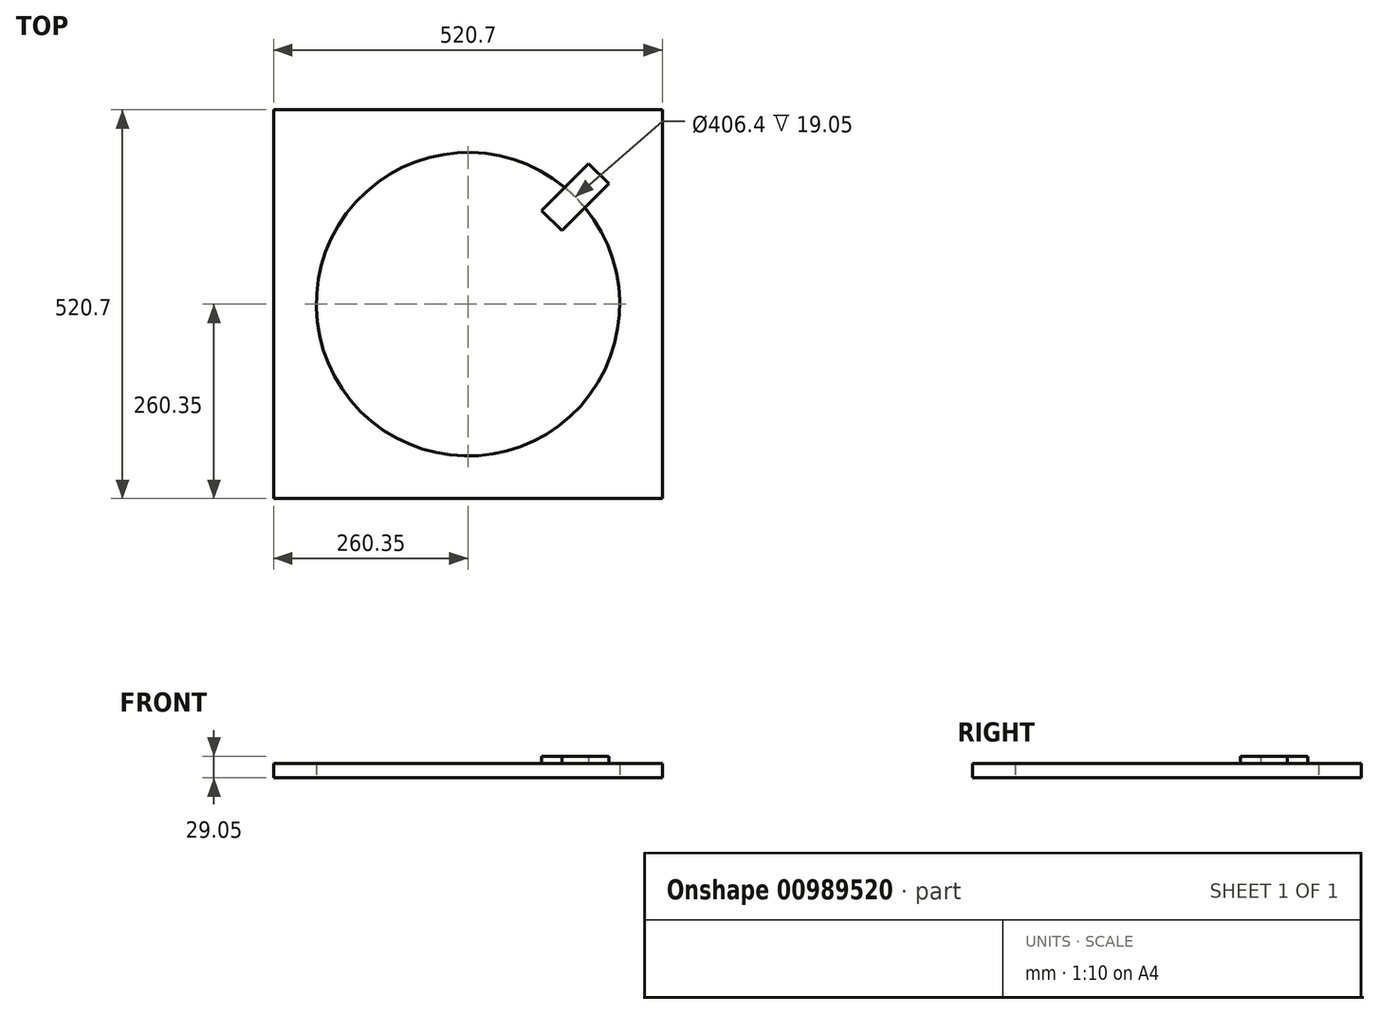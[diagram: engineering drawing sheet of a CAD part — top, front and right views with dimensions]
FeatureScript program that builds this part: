
annotation { "Feature Type Name" : "Feature", "Feature Type Description" : "" }
export const myFeature = defineFeature(function(context is Context, id is Id, definition is map)
    precondition{}
    {
        {
            var Q0;
            Q0=qCreatedBy(makeId("Top.planeOp"),FACE);
            var sketch = newSketch(context, id + "F0", { "sketchPlane" : qUnion([Q0])});
            skLineSegment(sketch, "E0.bottom", {"start": v(-260.35, -260.35) * mm, "end": v(260.35, -260.35) * mm});
            skLineSegment(sketch, "E0.top", {"start": v(-260.35, 260.35) * mm, "end": v(260.35, 260.35) * mm});
            skLineSegment(sketch, "E0.left", {"start": v(-260.35, -260.35) * mm, "end": v(-260.35, 260.35) * mm});
            skLineSegment(sketch, "E0.right", {"start": v(260.35, -260.35) * mm, "end": v(260.35, 260.35) * mm});
            skPoint(sketch, "E0.middle", {"position": v(0, 0) * mm});
            skCircle(sketch, "E1", {"center": v(0, 0) * mm, "radius": 203.2 * mm});
            skSolve(sketch);
        }
        {
            var Q0;
            Q0 = qSketchRegion(id + "F0", true);
            extrude(context, id + "F1", {"entities" : qUnion([Q0]), "depth" : 19.05 * mm, "offsetDistance" : 25.4 * mm});
        }
        {
            var Q0;
            Q0=makeQuery(id+"F1.opExtrude","CAP_FACE",FACE,{"disambiguationData":[OSD([sQuery(id+"F0.wireOp",EDGE,"E0.bottom"),sQuery(id+"F0.wireOp",EDGE,"E0.top"),sQuery(id+"F0.wireOp",EDGE,"E0.left"),sQuery(id+"F0.wireOp",EDGE,"E0.right"),sQuery(id+"F0.wireOp",EDGE,"E1")])],"isStart":false});
            var sketch = newSketch(context, id + "F2", { "sketchPlane" : qUnion([Q0])});
            skLineSegment(sketch, "E2", {"start": v(260.35, 260.35) * mm, "end": v(-260.35, -260.35) * mm, "construction": true});
            skLineSegment(sketch, "E3", {"start": v(125.65, 98.7) * mm, "end": v(188.5, 161.57) * mm});
            skLineSegment(sketch, "E4", {"start": v(188.5, 161.57) * mm, "end": v(161.57, 188.5) * mm});
            skLineSegment(sketch, "E5", {"start": v(161.57, 188.5) * mm, "end": v(98.7, 125.65) * mm});
            skLineSegment(sketch, "E6", {"start": v(98.7, 125.65) * mm, "end": v(125.65, 98.7) * mm});
            skSolve(sketch);
        }
        {
            var Q0;
            Q0 = qSketchRegion(id + "F2", true);
            extrude(context, id + "F3", {"entities" : qUnion([Q0]), "operationType" : NewBodyOperationType.ADD, "depth" : 10 * mm, "offsetDistance" : 25.4 * mm});
        }
    });
